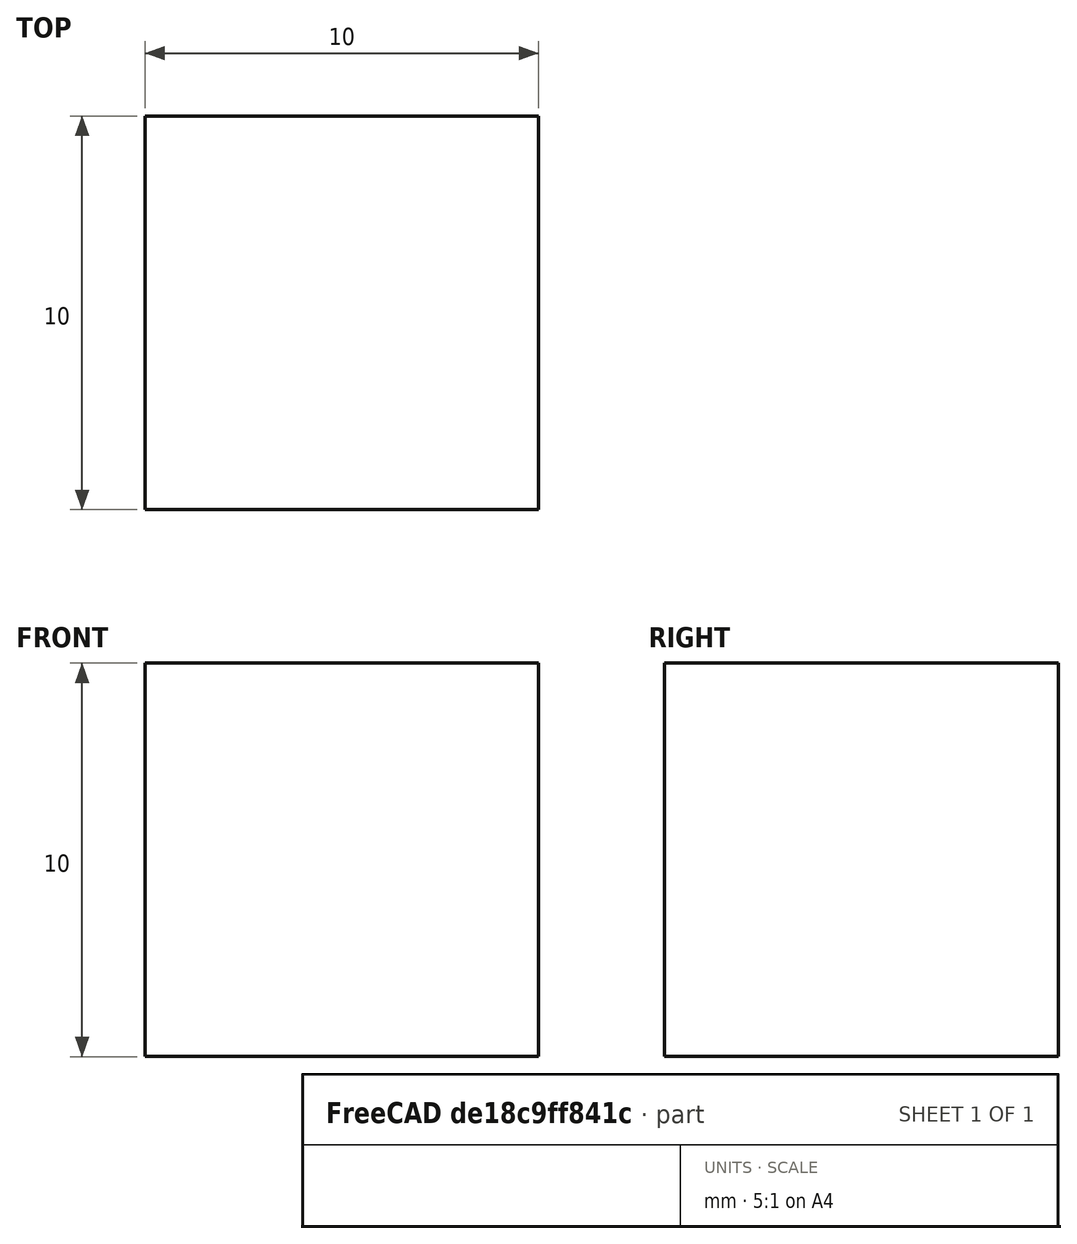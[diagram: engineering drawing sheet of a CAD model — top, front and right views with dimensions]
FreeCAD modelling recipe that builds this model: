
FCSTD DOCUMENT  (FreeCAD 1.1R44874 (Git))
Label: simple
License: All rights reserved
LicenseURL: https://en.wikipedia.org/wiki/All_rights_reserved
objects: Part::Box×1, App::LinkGroupPython×1, Part::FeaturePython×1, Sketcher::SketchObject×1
note: 4 computed .brp shape members not serialized (recipe doc carries the construction recipe); baked Part::Feature solids carry a one-line shape summary decoded from their .brp

FEATURE [Part::Box] Box  label="labeledBox"
  AttacherType = Attacher::AttachEngine3D
  Height = 10
  Length = 10
  Placement = pos=(1,2,0.0522433) rot=(0,0,1;0rad)
  Width = 10
FEATURE [App::LinkGroupPython] OpticalPointSource  label="src"  # WARN: FeaturePython — macro-defined, semantics opaque (R4)
  Divergence = -
  FanPhi0 = 0
  Fans = 2
  FocalLength = 0
  LinkMode = 0
  MaxIntersectionsScale = 1
  MaxRayLengthScale = 1
  PhiDomain = 0, 2*pi
  PhiResolutionNumericMode = 100
  PowerDensity = exp(-theta**2/(1e-2)**2)
  RadiusDomain = 0, 10
  RadiusResolutionNumericMode = 100000
  RandomNumberGeneratorMode = ?
  RaysPerFan = 20
  RaysPerIterationScale = 1
  RecordRays = false
  ThetaDomain = 0, pi/4
  ThetaResolutionNumericMode = 100000
  Wavelength = 500
FEATURE [Part::FeaturePython] OpticalSimulationSettings  label="cfg"  # WARN: FeaturePython — macro-defined, semantics opaque (R4)
  Active = true
  DistanceTolerance = 1e-06
  EnableStoreSingleShotData = false
  EndAfterHits = inf
  EndAfterIterations = inf
  EndAfterRays = 10000
  MaxIntersections = 100
  MaxRayLength = 236.818
  RaysPerIteration = 100
  SequentialMode = false
  ShowRaysInContinuousMode = true
  StoreHitFanIndex = false
  StoreHitInitDirection = false
  StoreHitInitPhi = false
  StoreHitInitPoint = false
  StoreHitInitPower = false
  StoreHitInitTheta = false
  StoreHitInitWavelength = false
  StoreHitRayIndex = false
  StoreHitTotalFanCount = false
  StoreHitTotalRaysInFan = false
  WorkerProcessCount = num_cpus
FEATURE [Sketcher::SketchObject] Sketch
  ArcFitTolerance = 1e-06
  AttachmentSupport = -> [OpticalSimulationSettings]
  ExternalTypes = [0]
  FullyConstrained = true
  MakeInternals = false
  MapMode = 2
  _ExternalGeoVersion = 1
  sketch-geometry (1):
    g0: Circle CenterX=0 CenterY=0 CenterZ=0 NormalX=0 NormalY=0 NormalZ=1 AngleXU=0 Radius=2.86439
  constraints (2):
    c: Coincident(g0,g-1)
    c: Radius(g0) = 2.86439  'namedConstraint'
